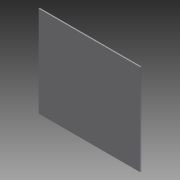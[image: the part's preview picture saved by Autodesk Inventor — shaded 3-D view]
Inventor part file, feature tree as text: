
AUTODESK INVENTOR PART (.ipt)
format: ipt  version: 2011 (Build 150239000, 239)  size: 65,024 bytes
history: native  units: in
note: dims shown in document units (in); Inventor stores cm internally (conversion verified against a paired STEP export)
features: extrude x1, sketch x1
ambient origin geometry x8: Origin, YZ Plane, XZ Plane, XY Plane, X Axis, Y Axis, Z Axis, Center Point
bodies: Solid1 (feature_tree)
feature tree (2):
  extrude  "Extrusion1"  Depth=18.14in
  sketch  "Sketch1"  dims[d0=20.248in d1=18.14in d2=0.25in d3=0.0in]
